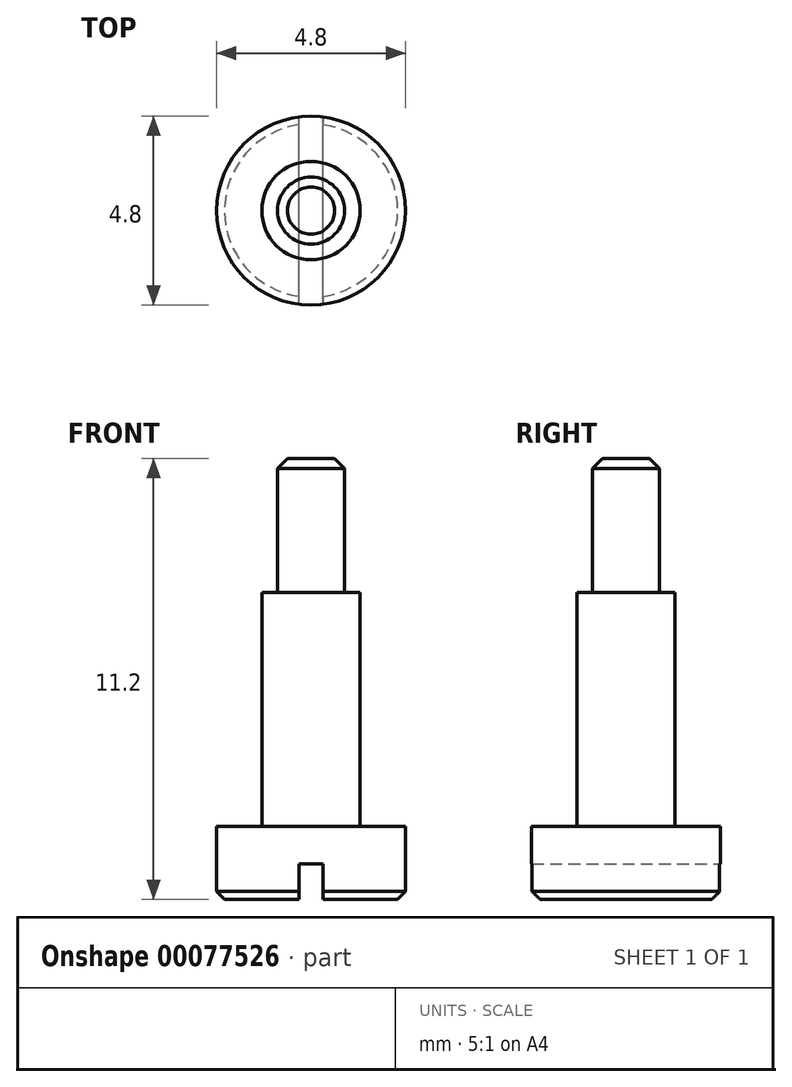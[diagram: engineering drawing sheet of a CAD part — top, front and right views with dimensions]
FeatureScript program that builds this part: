
annotation { "Feature Type Name" : "Feature", "Feature Type Description" : "" }
export const myFeature = defineFeature(function(context is Context, id is Id, definition is map)
    precondition{}
    {
        {
            var Q0;
            Q0=qCreatedBy(makeId("Front.planeOp"),FACE);
            var sketch = newSketch(context, id + "F0", { "sketchPlane" : qUnion([Q0])});
            skLineSegment(sketch, "E0", {"start": v(0, 0) * mm, "end": v(2.4, 0) * mm});
            skLineSegment(sketch, "E1", {"start": v(2.4, 0) * mm, "end": v(2.4, 1.85) * mm});
            skLineSegment(sketch, "E2", {"start": v(2.4, 1.85) * mm, "end": v(1.25, 1.85) * mm});
            skLineSegment(sketch, "E3", {"start": v(1.25, 1.85) * mm, "end": v(1.25, 7.8) * mm});
            skLineSegment(sketch, "E4", {"start": v(1.25, 7.8) * mm, "end": v(0.85, 7.8) * mm});
            skLineSegment(sketch, "E5", {"start": v(0.85, 7.8) * mm, "end": v(0.85, 11.2) * mm});
            skLineSegment(sketch, "E6", {"start": v(0.85, 11.2) * mm, "end": v(0, 11.2) * mm});
            skLineSegment(sketch, "E7", {"start": v(0, 11.2) * mm, "end": v(0, 0) * mm});
            skSolve(sketch);
        }
        {
            var Q0;
            Q0=makeQuery(id+"F0.imprint","IMPRINT",FACE,{"disambiguationData":[TD([[makeQuery(id+"F0.imprint","IMPRINT",EDGE,{"derivedFrom":sQuery(id+"F0.wireOp",EDGE,"E0")}),1.0]])]});
            var Q1;
            Q1=sQuery(id+"F0.wireOp",EDGE,"E7");
            revolve(context, id + "F1", {"entities" : qUnion([Q0]), "axis" : qUnion([Q1]), "revolveType" : RevolveType.FULL});
        }
        {
            var Q0;
            Q0=makeQuery(id+"F1.opRevolve","SWEPT_EDGE",EDGE,{"disambiguationData":[OSD([sQuery(id+"F0.wireOp",EDGE,"E5"),sQuery(id+"F0.wireOp",EDGE,"E6")])]});
            chamfer(context, id + "F2", {"entities" : qUnion([Q0]), "width" : 0.25 * mm, "tangentPropagation" : true});
        }
        {
            var Q0;
            Q0=makeQuery(id+"F1.opRevolve","SWEPT_FACE",FACE,{"disambiguationData":[OSD([sQuery(id+"F0.wireOp",EDGE,"E0")])]});
            var sketch = newSketch(context, id + "F3", { "sketchPlane" : qUnion([Q0])});
            skLineSegment(sketch, "E8", {"start": v(-0.3, 2.38) * mm, "end": v(-0.3, -2.38) * mm});
            skLineSegment(sketch, "E9", {"start": v(0.3, 2.38) * mm, "end": v(0.3, -2.38) * mm});
            skSolve(sketch);
        }
        {
            var Q0;
            {var subQ2=sQuery(id+"F3.wireOp",EDGE,"E8");Q0=makeQuery(id+"F3.imprint","IMPRINT",FACE,{"disambiguationData":[TD([[makeQuery(id+"F3.imprint","IMPRINT",EDGE,{"derivedFrom":subQ2}),1.0]])]});}
            extrude(context, id + "F4", {"entities" : qUnion([Q0]), "operationType" : NewBodyOperationType.REMOVE, "oppositeDirection" : true, "depth" : 0.9 * mm});
        }
        {
            var Q0;
            {var subQ0=sQuery(id+"F0.wireOp",EDGE,"E0");var subQ1=sQuery(id+"F0.wireOp",EDGE,"E1");var subQ2=makeQuery(id+"F1.opRevolve","SWEPT_EDGE",EDGE,{"disambiguationData":[OSD([subQ0,subQ1])]});Q0=qUnion([makeQuery(id+"F4.boolean.opBoolean","SPLIT",EDGE,{"disambiguationData":[TD([makeQuery(id+"F4.opExtrude","SWEPT_FACE",FACE,{"disambiguationData":[OSD([sQuery(id+"F3.wireOp",EDGE,"E9")])]})])],"derivedFrom":subQ2}),makeQuery(id+"F4.boolean.opBoolean","SPLIT",EDGE,{"disambiguationData":[TD([makeQuery(id+"F4.opExtrude","SWEPT_FACE",FACE,{"disambiguationData":[OSD([sQuery(id+"F3.wireOp",EDGE,"E8")])]})])],"derivedFrom":subQ2})]);}
            chamfer(context, id + "F5", {"entities" : qUnion([Q0]), "width" : 0.2 * mm, "tangentPropagation" : true});
        }
    });
